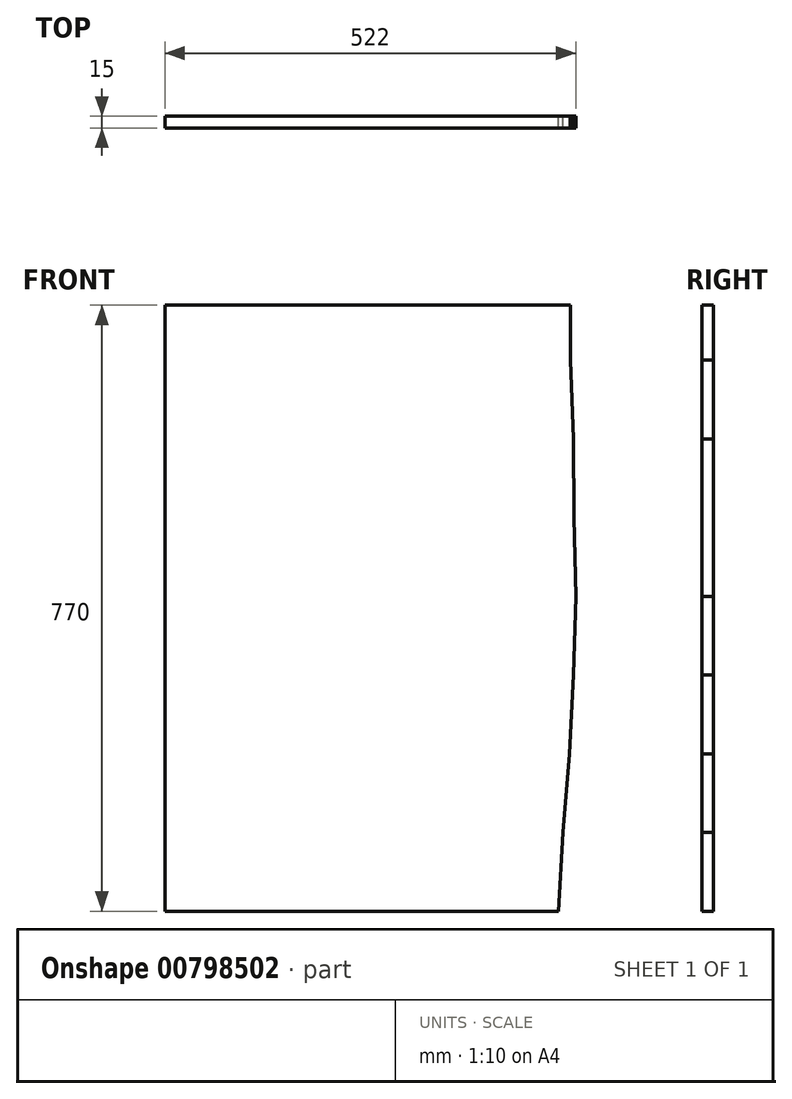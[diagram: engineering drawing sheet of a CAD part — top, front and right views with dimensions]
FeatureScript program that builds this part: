
annotation { "Feature Type Name" : "Feature", "Feature Type Description" : "" }
export const myFeature = defineFeature(function(context is Context, id is Id, definition is map)
    precondition{}
    {
        {
            var Q0;
            Q0=qCreatedBy(makeId("Front.planeOp"),FACE);
            var sketch = newSketch(context, id + "F0", { "sketchPlane" : qUnion([Q0])});
            skLineSegment(sketch, "E0", {"start": v(0, 0) * mm, "end": v(0, -770) * mm});
            skLineSegment(sketch, "E1", {"start": v(0, -770) * mm, "end": v(500, -770) * mm});
            skLineSegment(sketch, "E2", {"start": v(0, 0) * mm, "end": v(515, 0) * mm});
            skLineSegment(sketch, "E3", {"start": v(500, -770) * mm, "end": v(506, -670) * mm});
            skLineSegment(sketch, "E4", {"start": v(506, -670) * mm, "end": v(514, -570) * mm});
            skLineSegment(sketch, "E5", {"start": v(514, -570) * mm, "end": v(519, -470) * mm});
            skLineSegment(sketch, "E6", {"start": v(519, -470) * mm, "end": v(522, -370) * mm});
            skLineSegment(sketch, "E7", {"start": v(522, -370) * mm, "end": v(520, -270) * mm});
            skLineSegment(sketch, "E8", {"start": v(520, -270) * mm, "end": v(519, -170) * mm});
            skLineSegment(sketch, "E9", {"start": v(519, -170) * mm, "end": v(515, -70) * mm});
            skLineSegment(sketch, "E10", {"start": v(515, 0) * mm, "end": v(515, -70) * mm});
            skSolve(sketch);
        }
        {
            var Q0;
            Q0=makeQuery(id+"F0.imprint","IMPRINT",FACE,{"disambiguationData":[TD([[makeQuery(id+"F0.imprint","IMPRINT",EDGE,{"derivedFrom":sQuery(id+"F0.wireOp",EDGE,"E0")}),1.0]])]});
            extrude(context, id + "F1", {"entities" : qUnion([Q0]), "depth" : 15 * mm, "offsetDistance" : 25 * mm});
        }
    });
